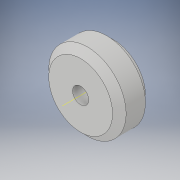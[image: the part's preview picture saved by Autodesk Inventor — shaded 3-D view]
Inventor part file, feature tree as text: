
AUTODESK INVENTOR PART (.ipt)
format: ipt  version: 2019 (Build 230136000, 136)  size: 112,640 bytes
history: native  units: in
note: dims shown in document units (in); Inventor stores cm internally (conversion verified against a paired STEP export)
features: revolve x1, other x1, sketch x1
ambient origin geometry x8: Origin, YZ Plane, XZ Plane, XY Plane, X Axis, Y Axis, Z Axis, Center Point
bodies: Solid1 (feature_tree)
feature tree (3):
  revolve  "Revolution1"  [1 undecoded]
  other  "Work Axis1"
  sketch  "Sketch2"  dims[d5=0.2362in d8=0.4016in d11=90.0deg]
note: 1 required parameter value undecoded (feature->parameter linkage not recoverable at this tier; creation-order binding heuristic only, values carry confidence <= 0.55)
